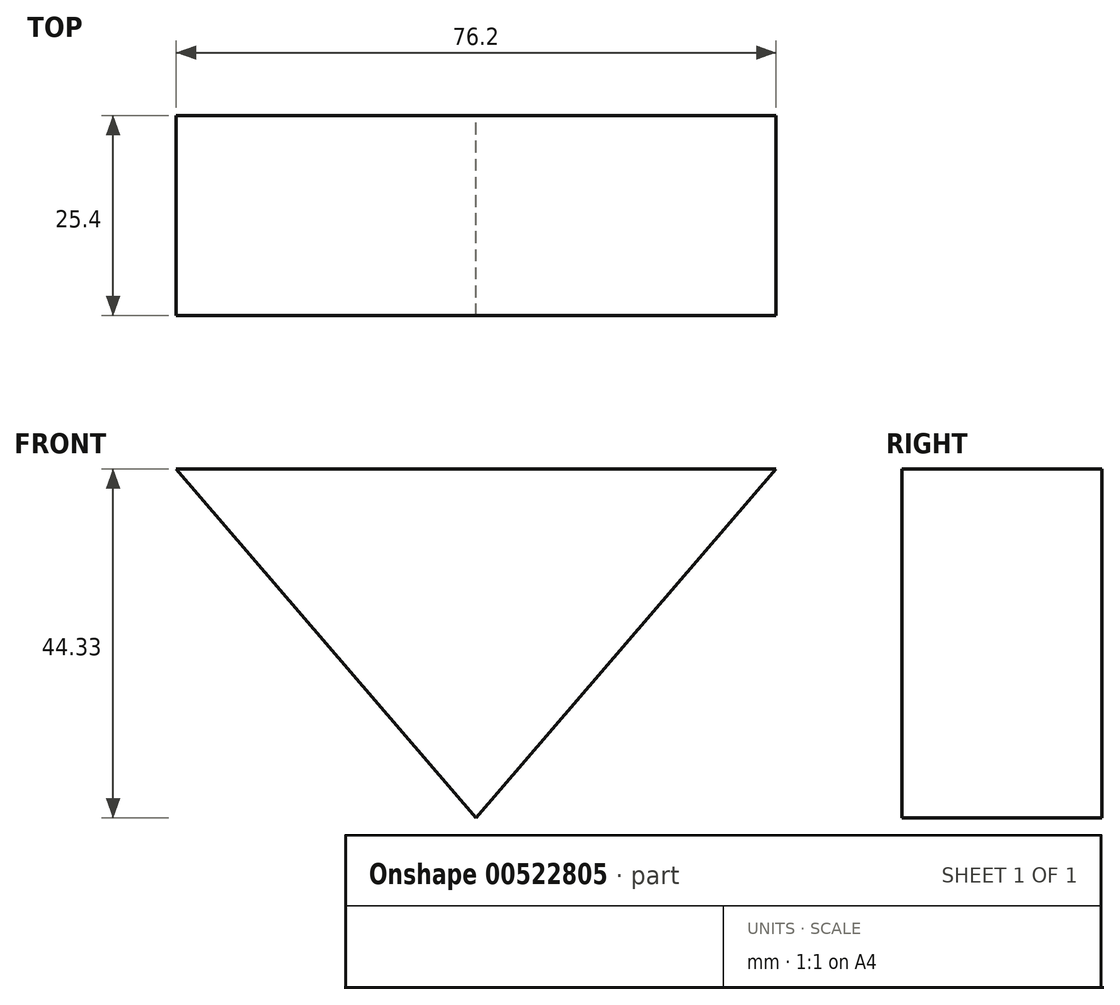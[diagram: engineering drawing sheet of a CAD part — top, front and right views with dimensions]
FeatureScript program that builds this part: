
annotation { "Feature Type Name" : "Feature", "Feature Type Description" : "" }
export const myFeature = defineFeature(function(context is Context, id is Id, definition is map)
    precondition{}
    {
        {
            var Q0;
            Q0=qCreatedBy(makeId("Front.planeOp"),FACE);
            var sketch = newSketch(context, id + "F0", { "sketchPlane" : qUnion([Q0])});
            skLineSegment(sketch, "E0", {"start": v(0, 0) * mm, "end": v(-38.1, 44.33) * mm});
            skLineSegment(sketch, "E1", {"start": v(-38.1, 44.33) * mm, "end": v(38.1, 44.33) * mm});
            skLineSegment(sketch, "E2", {"start": v(0, 0) * mm, "end": v(38.1, 44.33) * mm});
            skSolve(sketch);
        }
        {
            var Q0;
            Q0 = qSketchRegion(id + "F0", true);
            extrude(context, id + "F1", {"entities" : qUnion([Q0]), "depth" : 25.4 * mm, "offsetDistance" : 25.4 * mm});
        }
    });
